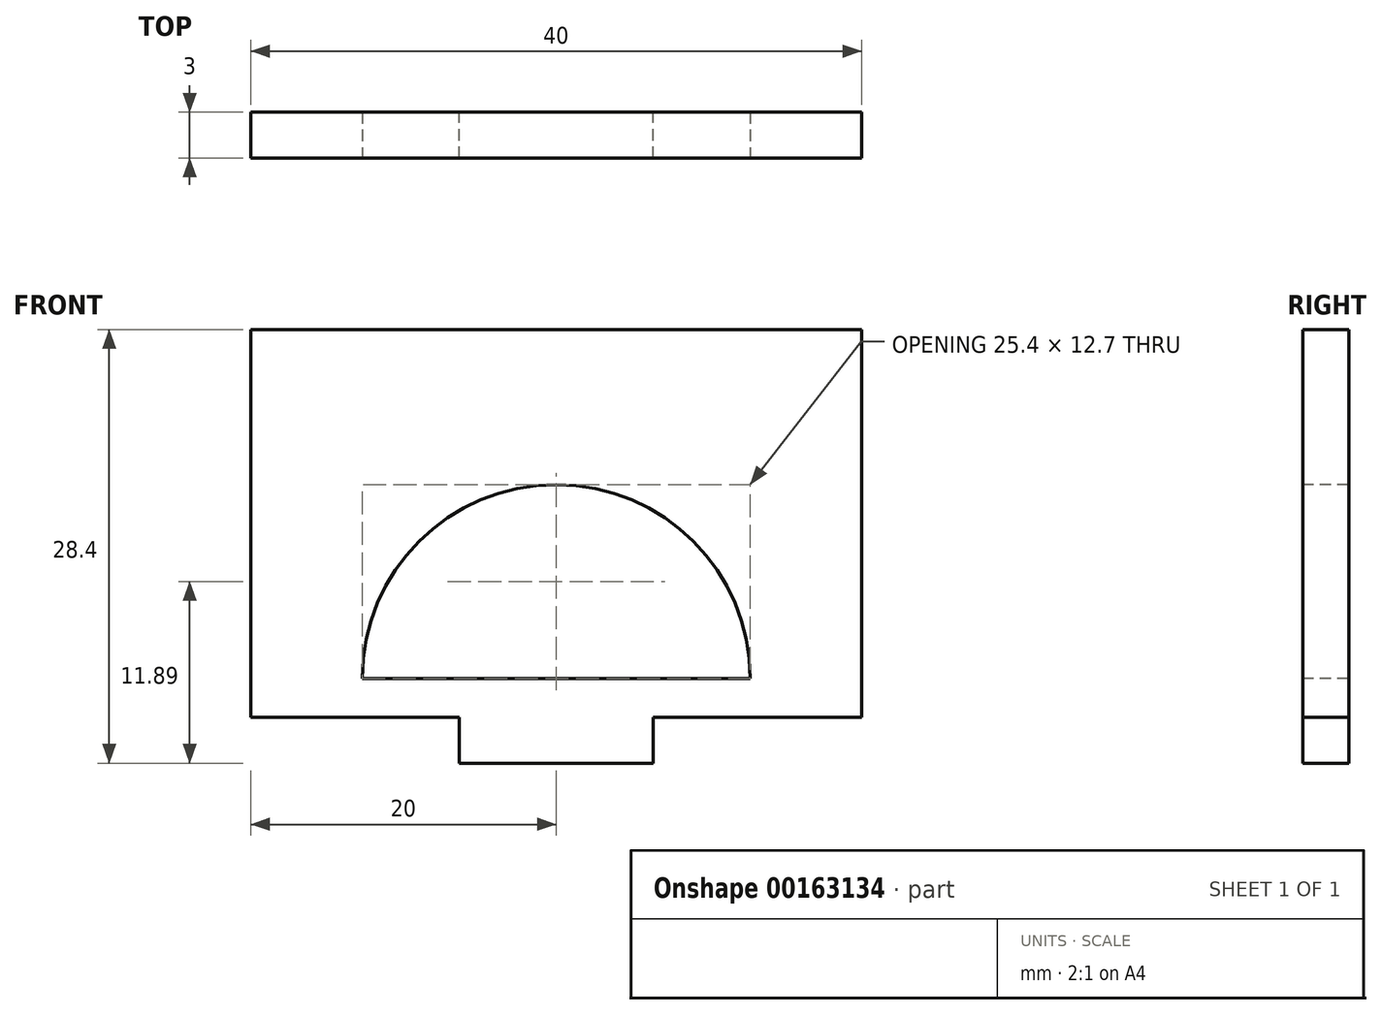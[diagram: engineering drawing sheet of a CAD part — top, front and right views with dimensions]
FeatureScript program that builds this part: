
annotation { "Feature Type Name" : "Feature", "Feature Type Description" : "" }
export const myFeature = defineFeature(function(context is Context, id is Id, definition is map)
    precondition{}
    {
        {
            var Q0;
            Q0=qCreatedBy(makeId("Front.planeOp"),FACE);
            var sketch = newSketch(context, id + "F0", { "sketchPlane" : qUnion([Q0])});
            skLineSegment(sketch, "E0.bottom", {"start": v(-20, 12.7) * mm, "end": v(20, 12.7) * mm});
            skLineSegment(sketch, "E0.top", {"start": v(-20, -12.7) * mm, "end": v(-6.35, -12.7) * mm});
            skLineSegment(sketch, "E0.left", {"start": v(-20, 12.7) * mm, "end": v(-20, -12.7) * mm});
            skLineSegment(sketch, "E0.right", {"start": v(20, 12.7) * mm, "end": v(20, -12.7) * mm});
            skPoint(sketch, "E0.middle", {"position": v(0, 0) * mm});
            skLineSegment(sketch, "E1", {"start": v(-6.35, -12.7) * mm, "end": v(-6.35, -15.7) * mm});
            skLineSegment(sketch, "E2", {"start": v(-6.35, -15.7) * mm, "end": v(6.35, -15.7) * mm});
            skLineSegment(sketch, "E3", {"start": v(6.35, -15.7) * mm, "end": v(6.35, -12.7) * mm});
            skLineSegment(sketch, "E4", {"start": v(0, 0) * mm, "end": v(0, -15.7) * mm, "construction": true});
            skLineSegment(sketch, "E5.trimOffspring", {"start": v(6.35, -12.7) * mm, "end": v(20, -12.7) * mm});
            skSolve(sketch);
        }
        {
            var Q0;
            Q0 = qSketchRegion(id + "F0", true);
            extrude(context, id + "F1", {"entities" : qUnion([Q0]), "depth" : 3 * mm});
        }
        {
            var Q0;
            Q0=makeQuery(id+"F1.opExtrude","CAP_FACE",FACE,{"disambiguationData":[OSD([sQuery(id+"F0.wireOp",EDGE,"E0.bottom"),sQuery(id+"F0.wireOp",EDGE,"E0.top"),sQuery(id+"F0.wireOp",EDGE,"E0.left"),sQuery(id+"F0.wireOp",EDGE,"E0.right"),sQuery(id+"F0.wireOp",EDGE,"E1"),sQuery(id+"F0.wireOp",EDGE,"E2"),sQuery(id+"F0.wireOp",EDGE,"E3"),sQuery(id+"F0.wireOp",EDGE,"E5.trimOffspring")])],"isStart":false});
            var sketch = newSketch(context, id + "F2", { "sketchPlane" : qUnion([Q0])});
            skArc(sketch, "E6", {"start": v(12.7, -10.16) * mm, "mid": v(0, 2.54) * mm, "end": v(-12.7, -10.16) * mm});
            skLineSegment(sketch, "E7", {"start": v(12.7, -10.16) * mm, "end": v(-12.7, -10.16) * mm});
            skSolve(sketch);
        }
        {
            var Q0;
            Q0 = qSketchRegion(id + "F2", true);
            extrude(context, id + "F3", {"entities" : qUnion([Q0]), "operationType" : NewBodyOperationType.REMOVE, "endBound" : BoundingType.UP_TO_NEXT, "oppositeDirection" : true, "depth" : 25.4 * mm});
        }
    });
